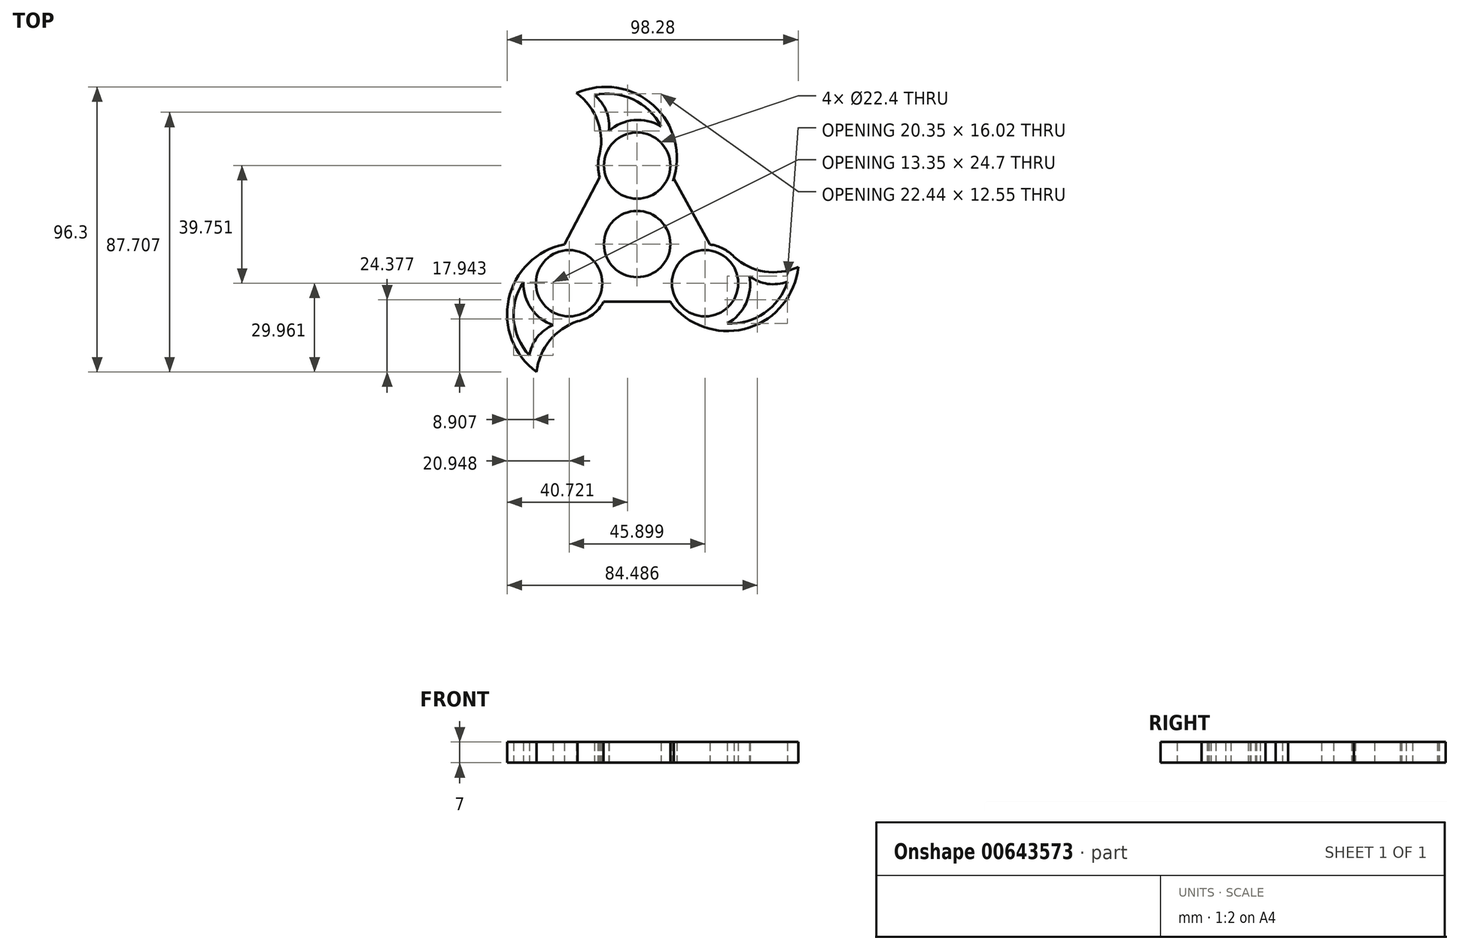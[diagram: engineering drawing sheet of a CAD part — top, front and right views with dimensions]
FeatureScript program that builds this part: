
annotation { "Feature Type Name" : "Feature", "Feature Type Description" : "" }
export const myFeature = defineFeature(function(context is Context, id is Id, definition is map)
    precondition{}
    {
        {
            var Q0;
            Q0=qCreatedBy(makeId("Top.planeOp"),FACE);
            var sketch = newSketch(context, id + "F0", { "sketchPlane" : qUnion([Q0])});
            skCircle(sketch, "E0", {"center": v(0, 0) * mm, "radius": 11.2 * mm});
            skCircle(sketch, "E1", {"center": v(0, 26.5) * mm, "radius": 11.2 * mm});
            skArc(sketch, "E2", {"start": v(12.16, 21.36) * mm, "mid": v(12.83, 23.4) * mm, "end": v(13.16, 25.53) * mm});
            skArc(sketch, "E3.1.0", {"start": v(-20.07, -26.13) * mm, "mid": v(-14.96, -23.75) * mm, "end": v(-11.3, -19.46) * mm});
            skCircle(sketch, "E3.1.1", {"center": v(-22.95, -13.25) * mm, "radius": 11.2 * mm});
            skArc(sketch, "E3.2.0", {"start": v(11.3, -19.46) * mm, "mid": v(13.11, -22.05) * mm, "end": v(15.48, -24.14) * mm});
            skCircle(sketch, "E3.2.1", {"center": v(22.95, -13.25) * mm, "radius": 11.2 * mm});
            skArc(sketch, "E4", {"start": v(12.16, 21.36) * mm, "mid": v(5.55, 46.86) * mm, "end": v(-20.47, 50.97) * mm});
            skArc(sketch, "E5", {"start": v(-12.95, 29.06) * mm, "mid": v(-13.23, 41.21) * mm, "end": v(-20.47, 50.97) * mm});
            skArc(sketch, "E6.1.0", {"start": v(-24.58, -0.15) * mm, "mid": v(-43.36, -18.62) * mm, "end": v(-33.91, -43.21) * mm});
            skArc(sketch, "E6.1.1", {"start": v(-18.7, -25.74) * mm, "mid": v(-29.08, -32.06) * mm, "end": v(-33.91, -43.21) * mm});
            skArc(sketch, "E6.2.0", {"start": v(12.41, -21.2) * mm, "mid": v(37.8, -28.23) * mm, "end": v(54.38, -7.76) * mm});
            skArc(sketch, "E6.2.1", {"start": v(31.64, -3.32) * mm, "mid": v(42.3, -9.15) * mm, "end": v(54.38, -7.76) * mm});
            skLineSegment(sketch, "E7", {"start": v(-12.61, 22.6) * mm, "end": v(-24.58, -0.15) * mm});
            skLineSegment(sketch, "E8", {"start": v(12.16, 22.6) * mm, "end": v(24.55, -0.15) * mm});
            skLineSegment(sketch, "E9", {"start": v(-11.3, -19.46) * mm, "end": v(11.3, -19.46) * mm});
            skArc(sketch, "E10", {"start": v(37.89, -10.82) * mm, "mid": v(44.28, -13.46) * mm, "end": v(51.13, -12.53) * mm});
            skArc(sketch, "E11", {"start": v(30.41, -26.84) * mm, "mid": v(43.03, -23.27) * mm, "end": v(50.76, -12.68) * mm});
            skArc(sketch, "E12", {"start": v(30.41, -26.84) * mm, "mid": v(36.74, -20.04) * mm, "end": v(37.89, -10.82) * mm});
            skArc(sketch, "E13.1.0", {"start": v(8.04, 39.76) * mm, "mid": v(-1.36, 48.9) * mm, "end": v(-14.4, 50.3) * mm});
            skArc(sketch, "E13.1.1", {"start": v(8.04, 39.76) * mm, "mid": v(-1.01, 41.84) * mm, "end": v(-9.57, 38.22) * mm});
            skArc(sketch, "E13.1.2", {"start": v(-9.57, 38.22) * mm, "mid": v(-10.48, 45.08) * mm, "end": v(-14.7, 50.54) * mm});
            skArc(sketch, "E13.2.0", {"start": v(-38.45, -12.92) * mm, "mid": v(-41.66, -25.63) * mm, "end": v(-36.36, -37.62) * mm});
            skArc(sketch, "E13.2.1", {"start": v(-38.45, -12.92) * mm, "mid": v(-35.73, -21.8) * mm, "end": v(-28.32, -27.4) * mm});
            skArc(sketch, "E13.2.2", {"start": v(-28.32, -27.4) * mm, "mid": v(-33.8, -31.61) * mm, "end": v(-36.42, -38.01) * mm});
            skArc(sketch, "E14.trimOffspring", {"start": v(-12.6, 30.44) * mm, "mid": v(-13.2, 26.52) * mm, "end": v(-12.61, 22.6) * mm});
            skArc(sketch, "E15.trimOffspring", {"start": v(-24.58, -0.15) * mm, "mid": v(-26.68, -0.58) * mm, "end": v(-28.68, -1.35) * mm});
            skArc(sketch, "E16.trimOffspring", {"start": v(32.68, -4.33) * mm, "mid": v(28.99, -1.51) * mm, "end": v(24.55, -0.15) * mm});
            skSolve(sketch);
        }
        {
            var Q0;
            Q0=makeQuery(id+"F0.imprint","IMPRINT",FACE,{"disambiguationData":[TD([[makeQuery(id+"F0.imprint","IMPRINT",EDGE,{"derivedFrom":sQuery(id+"F0.wireOp",EDGE,"E0")}),-1.0]])]});
            extrude(context, id + "F1", {"entities" : qUnion([Q0]), "depth" : 7 * mm, "offsetDistance" : 25 * mm});
        }
    });
